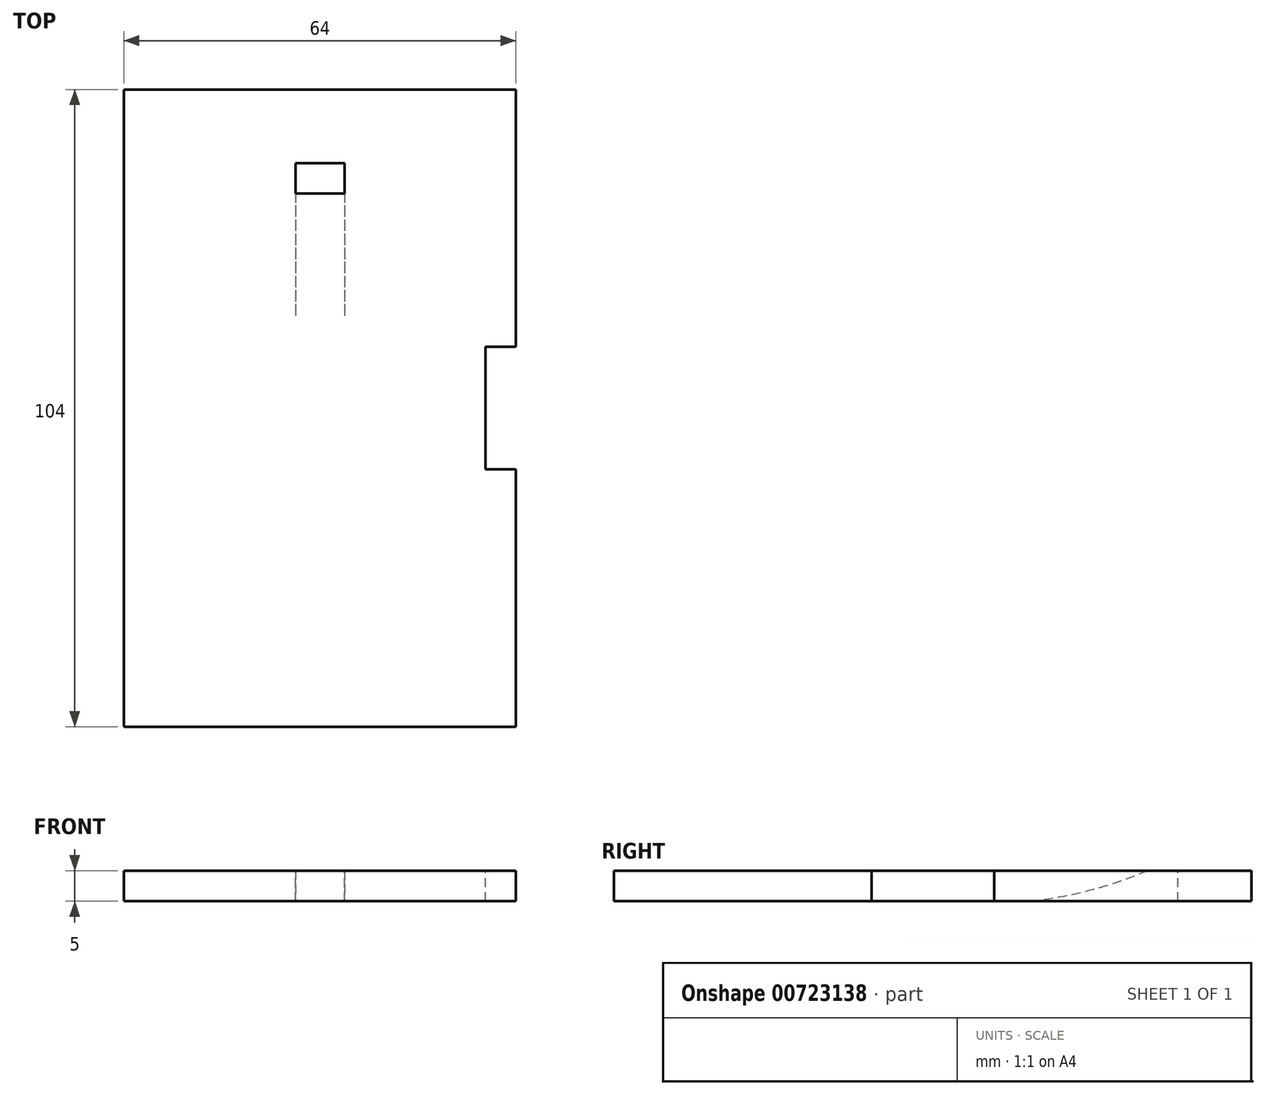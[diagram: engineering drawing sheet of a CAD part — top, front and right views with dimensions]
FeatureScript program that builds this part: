
annotation { "Feature Type Name" : "Feature", "Feature Type Description" : "" }
export const myFeature = defineFeature(function(context is Context, id is Id, definition is map)
    precondition{}
    {
        {
            var Q0;
            Q0=qCreatedBy(makeId("Top.planeOp"),FACE);
            var sketch = newSketch(context, id + "F0", { "sketchPlane" : qUnion([Q0])});
            skLineSegment(sketch, "E0.bottom", {"start": v(32, 52) * mm, "end": v(-32, 52) * mm});
            skLineSegment(sketch, "E0.top", {"start": v(32, -52) * mm, "end": v(-32, -52) * mm});
            skLineSegment(sketch, "E0.left", {"start": v(32, 52) * mm, "end": v(32, -52) * mm});
            skLineSegment(sketch, "E0.right", {"start": v(-32, 52) * mm, "end": v(-32, -52) * mm});
            skPoint(sketch, "E1", {"position": v(32, 0) * mm});
            skPoint(sketch, "E2", {"position": v(0, 52) * mm});
            skSolve(sketch);
        }
        {
            var Q0;
            Q0 = qSketchRegion(id + "F0", true);
            extrude(context, id + "F1", {"entities" : qUnion([Q0]), "depth" : 5 * mm, "offsetDistance" : 25 * mm});
        }
        {
            var Q0;
            Q0=makeQuery(id+"F1.opExtrude","CAP_FACE",FACE,{"disambiguationData":[OSD([sQuery(id+"F0.wireOp",EDGE,"E0.bottom"),sQuery(id+"F0.wireOp",EDGE,"E0.top"),sQuery(id+"F0.wireOp",EDGE,"E0.left"),sQuery(id+"F0.wireOp",EDGE,"E0.right")])],"isStart":false});
            var sketch = newSketch(context, id + "F2", { "sketchPlane" : qUnion([Q0])});
            skLineSegment(sketch, "E3.bottom", {"start": v(32, 10) * mm, "end": v(27, 10) * mm});
            skLineSegment(sketch, "E3.top", {"start": v(32, -10) * mm, "end": v(27, -10) * mm});
            skLineSegment(sketch, "E3.left", {"start": v(32, 10) * mm, "end": v(32, -10) * mm});
            skLineSegment(sketch, "E3.right", {"start": v(27, 10) * mm, "end": v(27, -10) * mm});
            skPoint(sketch, "E4", {"position": v(27, 0) * mm});
            skSolve(sketch);
        }
        {
            var Q0;
            Q0 = qSketchRegion(id + "F2", true);
            extrude(context, id + "F3", {"entities" : qUnion([Q0]), "operationType" : NewBodyOperationType.REMOVE, "oppositeDirection" : true, "depth" : 25 * mm, "offsetDistance" : 25 * mm});
        }
        {
            var Q0;
            Q0=makeQuery(id+"F1.opExtrude","CAP_FACE",FACE,{"disambiguationData":[OSD([sQuery(id+"F0.wireOp",EDGE,"E0.bottom"),sQuery(id+"F0.wireOp",EDGE,"E0.top"),sQuery(id+"F0.wireOp",EDGE,"E0.left"),sQuery(id+"F0.wireOp",EDGE,"E0.right")])],"isStart":false});
            var sketch = newSketch(context, id + "F4", { "sketchPlane" : qUnion([Q0])});
            skLineSegment(sketch, "E5.bottom", {"start": v(22, -52) * mm, "end": v(-22, -52) * mm, "construction": true});
            skLineSegment(sketch, "E5.top", {"start": v(22, 28) * mm, "end": v(-22, 28) * mm, "construction": true});
            skLineSegment(sketch, "E5.left", {"start": v(22, -52) * mm, "end": v(22, 28) * mm, "construction": true});
            skLineSegment(sketch, "E5.right", {"start": v(-22, -52) * mm, "end": v(-22, 28) * mm, "construction": true});
            skPoint(sketch, "E6", {"position": v(0, -52) * mm});
            skSolve(sketch);
        }
        {
            var Q0;
            {var subQ3=sQuery(id+"F0.wireOp",EDGE,"E0.bottom");Q0=makeQuery(id+"F4.imprint","IMPRINT",FACE,{"disambiguationData":[TD([[makeQuery(id+"F4.imprint","IMPRINT",EDGE,{"derivedFrom":makeQuery(id+"F1.opExtrude","CAP_EDGE",EDGE,{"disambiguationData":[OSD([subQ3])],"isStart":false})}),1.0]])]});}
            var sketch = newSketch(context, id + "F5", { "sketchPlane" : qUnion([Q0])});
            skLineSegment(sketch, "E7.bottom", {"start": v(4, 40) * mm, "end": v(-4, 40) * mm});
            skLineSegment(sketch, "E7.top", {"start": v(4, 15) * mm, "end": v(-4, 15) * mm});
            skLineSegment(sketch, "E7.left", {"start": v(4, 40) * mm, "end": v(4, 15) * mm});
            skLineSegment(sketch, "E7.right", {"start": v(-4, 40) * mm, "end": v(-4, 15) * mm});
            skPoint(sketch, "E8", {"position": v(0, 15) * mm});
            skSolve(sketch);
        }
        {
            var Q0;
            Q0 = qSketchRegion(id + "F5", true);
            extrude(context, id + "F6", {"entities" : qUnion([Q0]), "operationType" : NewBodyOperationType.REMOVE, "oppositeDirection" : true, "depth" : 25 * mm, "offsetDistance" : 25 * mm});
        }
        {
            var Q0;
            Q0=makeQuery(id+"F6.boolean.opBoolean","COPY",FACE,{"derivedFrom":makeQuery(id+"F6.opExtrude","SWEPT_FACE",FACE,{"disambiguationData":[OSD([sQuery(id+"F5.wireOp",EDGE,"E7.left")])]})});
            var sketch = newSketch(context, id + "F7", { "sketchPlane" : qUnion([Q0])});
            skLineSegment(sketch, "E9", {"start": v(-35, 5) * mm, "end": v(-15, 5) * mm});
            skLineSegment(sketch, "E10", {"start": v(-15, 5) * mm, "end": v(-15, 0) * mm});
            skFitSpline(sketch, "E11", {"points": [v(-35, 5) * mm, v(-15, 0) * mm], "startDerivative": vector(21.03, -9.59) * mm, "endDerivative": vector(11.17, -0.02) * mm});
            skSolve(sketch);
        }
        {
            var Q0;
            Q0 = qSketchRegion(id + "F7", true);
            extrude(context, id + "F8", {"entities" : qUnion([Q0]), "operationType" : NewBodyOperationType.ADD, "depth" : 25 * mm, "offsetDistance" : 25 * mm});
        }
    });
